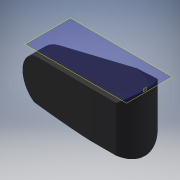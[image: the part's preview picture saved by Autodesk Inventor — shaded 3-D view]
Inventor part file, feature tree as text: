
AUTODESK INVENTOR PART (.ipt)
format: ipt  version: 2018 (Build 220112000, 112)  size: 159,232 bytes
history: native  units: in
note: dims shown in document units (in); Inventor stores cm internally (conversion verified against a paired STEP export)
features: extrude x3, sketch x3, plane x2
ambient origin geometry x8: Origin, YZ Plane, XZ Plane, XY Plane, X Axis, Y Axis, Z Axis, Center Point
bodies: Solid1 (feature_tree)
feature tree (8):
  extrude  "Extrusion1"  Depth=18.0in
  plane  "Work Plane1"
  extrude  "Extrusion2"  Depth=13.0in TaperAngle=0.0deg
  plane  "Work Plane2"
  extrude  "Extrusion3"  Depth=19.625in TaperAngle=0.0deg
  sketch  "Sketch1"  dims[d0=35.75in d2=18.0in]
  sketch  "Sketch2"  dims[d6=13.5in d7=13.0in d8=0.0in]
  sketch  "Sketch3"  dims[d9=-18.625in d14=19.625in d15=0.0in d16=90.0deg d17=90.0deg d18=40.875in d19=0.0in]
